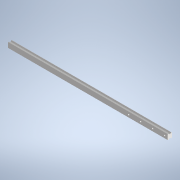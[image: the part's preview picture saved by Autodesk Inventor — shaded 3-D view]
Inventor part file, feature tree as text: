
AUTODESK INVENTOR PART (.ipt)
format: ipt  version: 2022 (Build 260153000, 153)  size: 161,280 bytes
history: native  units: mm (DEFAULTED — no unit token found)
features: other x21, sketch x2, extrude x1, hole x1, pattern_linear x1
ambient origin geometry x8: Origin, YZ Plane, XZ Plane, XY Plane, X Axis, Y Axis, Z Axis, Center Point
bodies: Solid1 (feature_tree)
feature tree (26):
  extrude  "Extrusion1"  Depth=10.0mm TaperAngle=0.0deg
  hole  "Hole1"  [1 undecoded]
  pattern_linear  "Rectangular Pattern1"  [2 undecoded]
  other  "4dummy_XY"
  other  "4dummy_YZ"
  other  "4dummy_ZX"
  other  "4dummy_X"
  other  "4dummy_Y"
  other  "4dummy_Z"
  other  "4dummy_Center"
  other  "4slide_XY"
  other  "4slide_YZ"
  other  "4slide_ZX"
  other  "4slide_X"
  other  "4slide_Y"
  other  "4slide_Z"
  other  "4slide_Center"
  other  "4track_XY"
  other  "4track_YZ"
  other  "4track_ZX"
  other  "4track_X"
  other  "4track_Y"
  other  "4track_Z"
  other  "4track_Center"
  sketch  "Sketch_18"  dims[d2=9.0mm d3=6.0mm d4=14.0mm d5=12.0mm d6=90.0deg d7=29.0mm d8=0.0mm d9=40.0mm d11=80.0mm d12=10.0mm d14=0.0mm d15=0.0mm]
  sketch  "Sketch2"  dims[d0=1066.8mm d1=0.0mm]
note: 3 required parameter values undecoded (feature->parameter linkage not recoverable at this tier; creation-order binding heuristic only, values carry confidence <= 0.55)
